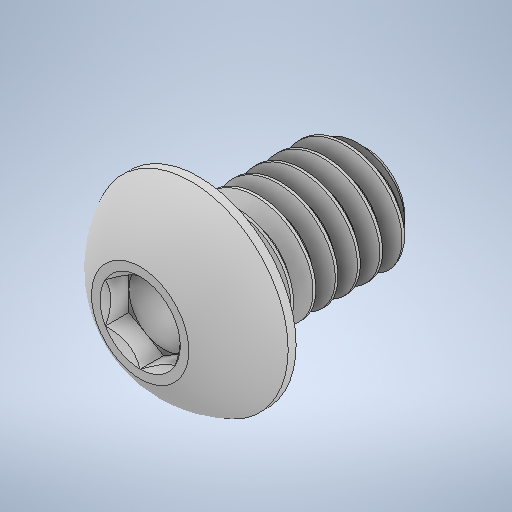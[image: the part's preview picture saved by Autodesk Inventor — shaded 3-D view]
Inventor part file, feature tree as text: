
AUTODESK INVENTOR PART (.ipt)
format: ipt  version: 2025.1 (Build 291241020, 241B)  size: 589,312 bytes
history: native  units: in
note: dims shown in document units (in); Inventor stores cm internally (conversion verified against a paired STEP export)
features: revolve x1
ambient origin geometry x8: Origin, YZ Plane, XZ Plane, XY Plane, X Axis, Y Axis, Z Axis, Center Point
bodies: Solid1 (feature_tree)
feature tree (1):
  revolve  "Revolve2"  [1 undecoded]
note: 1 required parameter value undecoded (feature->parameter linkage not recoverable at this tier; creation-order binding heuristic only, values carry confidence <= 0.55)
